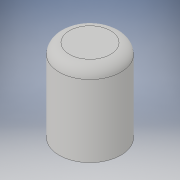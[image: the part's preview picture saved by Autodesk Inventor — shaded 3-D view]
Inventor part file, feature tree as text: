
AUTODESK INVENTOR PART (.ipt)
format: ipt  version: 2019.3 (Build 233278000, 278)  size: 117,760 bytes
history: native  units: mm
features: extrude x2, sketch x2, fillet x1
ambient origin geometry x8: Origin, YZ Plane, XZ Plane, XY Plane, X Axis, Y Axis, Z Axis, Center Point
bodies: Solid1 (feature_tree)
feature tree (5):
  extrude  "Extrusion1"  Depth=8.0mm TaperAngle=0.0deg
  extrude  "Extrusion2"  Depth=2.75mm
  fillet  "Fillet1"  Radius=2.5mm
  sketch  "Sketch1"  dims[d0=6.0mm d1=8.0mm d2=0.0mm]
  sketch  "Sketch2"  dims[d3=2.75mm d4=2.75mm d5=2.5mm d6=0.0mm d7=1.0mm]
